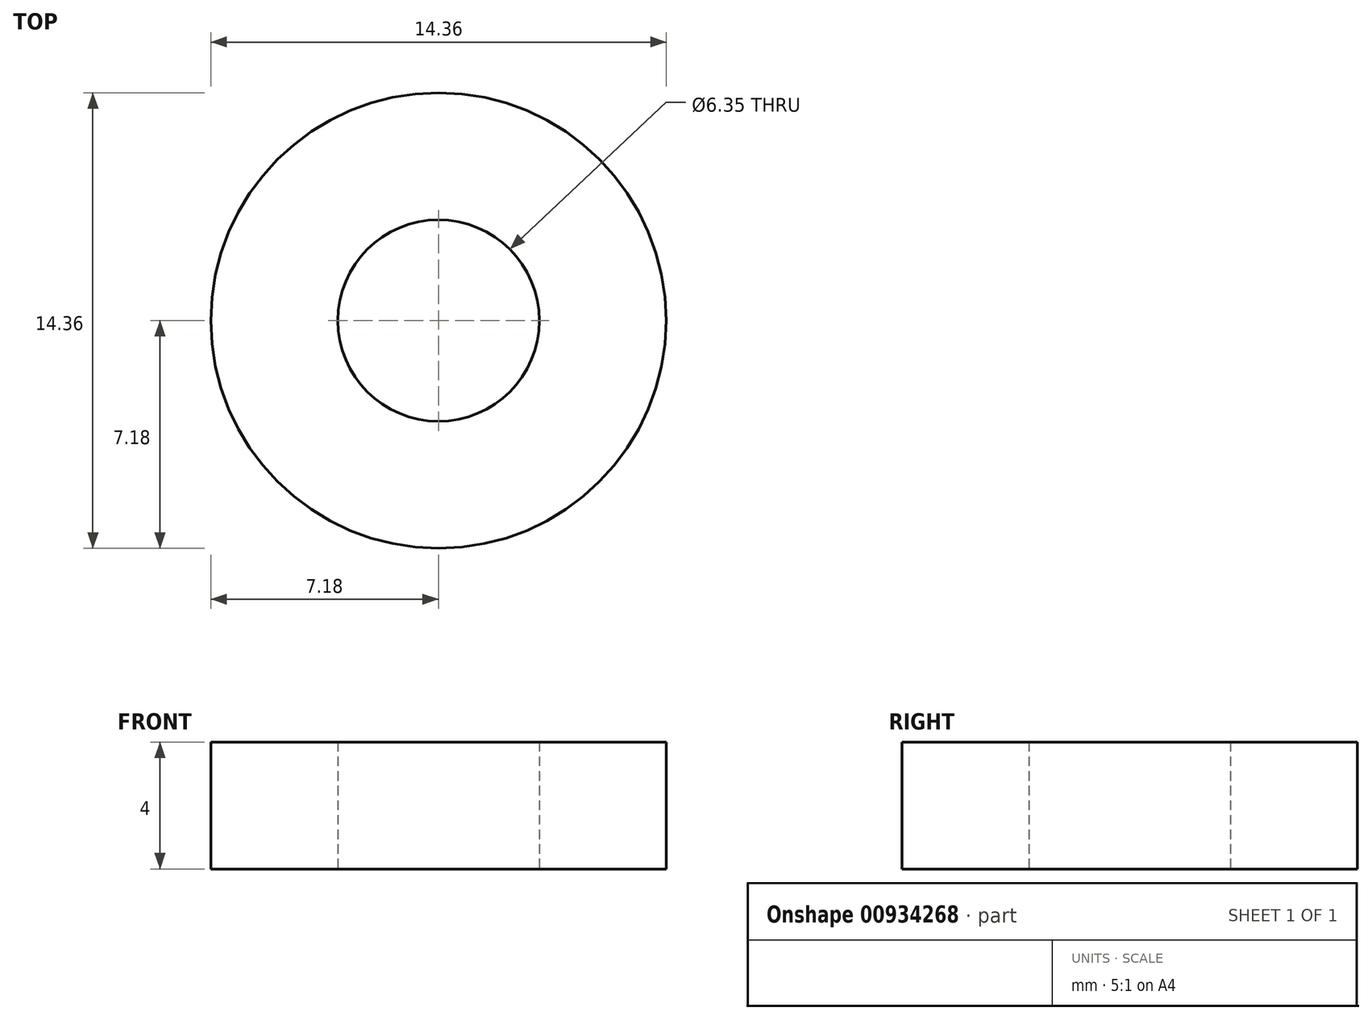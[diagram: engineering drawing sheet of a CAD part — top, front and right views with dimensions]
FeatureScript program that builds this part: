
annotation { "Feature Type Name" : "Feature", "Feature Type Description" : "" }
export const myFeature = defineFeature(function(context is Context, id is Id, definition is map)
    precondition{}
    {
        {
            var Q0;
            Q0=qCreatedBy(makeId("Top.planeOp"),FACE);
            var sketch = newSketch(context, id + "F0", { "sketchPlane" : qUnion([Q0])});
            skCircle(sketch, "E0", {"center": v(0, 0) * mm, "radius": 3.18 * mm});
            skCircle(sketch, "E1.0", {"center": v(0, 0) * mm, "radius": 7.18 * mm});
            skSolve(sketch);
        }
        {
            var Q0;
            Q0=makeQuery(id+"F0.imprint","IMPRINT",FACE,{"disambiguationData":[TD([[makeQuery(id+"F0.imprint","IMPRINT",EDGE,{"derivedFrom":sQuery(id+"F0.wireOp",EDGE,"E0")}),-1.0]])]});
            extrude(context, id + "F1", {"entities" : qUnion([Q0]), "depth" : 4 * mm, "offsetDistance" : 25 * mm});
        }
    });
